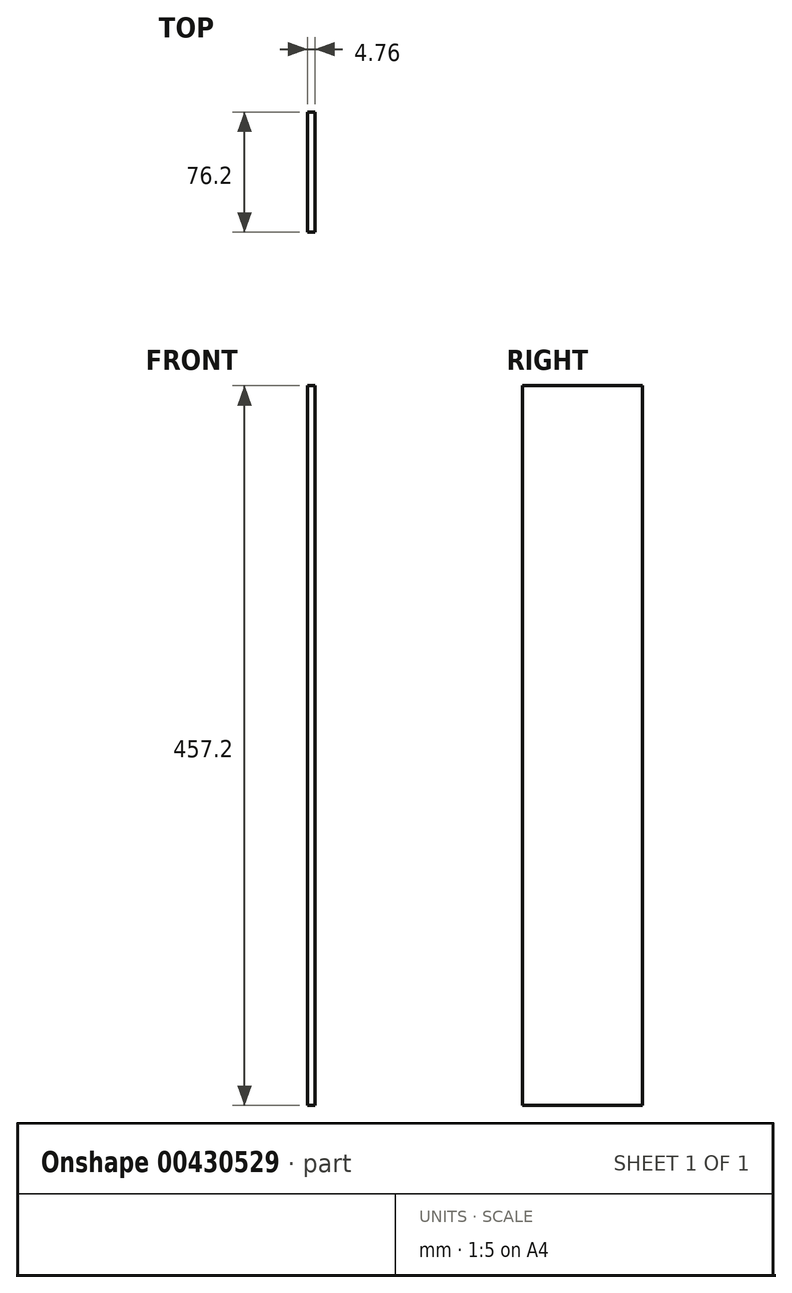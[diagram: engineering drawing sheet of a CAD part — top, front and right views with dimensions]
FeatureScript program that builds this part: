
annotation { "Feature Type Name" : "Feature", "Feature Type Description" : "" }
export const myFeature = defineFeature(function(context is Context, id is Id, definition is map)
    precondition{}
    {
        {
            var Q0;
            Q0=qCreatedBy(makeId("Right.planeOp"),FACE);
            var sketch = newSketch(context, id + "F0", { "sketchPlane" : qUnion([Q0])});
            skLineSegment(sketch, "E0.bottom", {"start": v(-51.93, 439.57) * mm, "end": v(24.27, 439.57) * mm});
            skLineSegment(sketch, "E0.top", {"start": v(-51.93, -17.63) * mm, "end": v(24.27, -17.63) * mm});
            skLineSegment(sketch, "E0.left", {"start": v(-51.93, 439.57) * mm, "end": v(-51.93, -17.63) * mm});
            skLineSegment(sketch, "E0.right", {"start": v(24.27, 439.57) * mm, "end": v(24.27, -17.63) * mm});
            skSolve(sketch);
        }
        {
            var Q0;
            Q0=makeQuery(id+"F0.imprint","IMPRINT",FACE,{"disambiguationData":[TD([[makeQuery(id+"F0.imprint","IMPRINT",EDGE,{"derivedFrom":sQuery(id+"F0.wireOp",EDGE,"E0.bottom")}),-1.0]])]});
            extrude(context, id + "F1", {"entities" : qUnion([Q0]), "depth" : 4.76 * mm});
        }
    });
